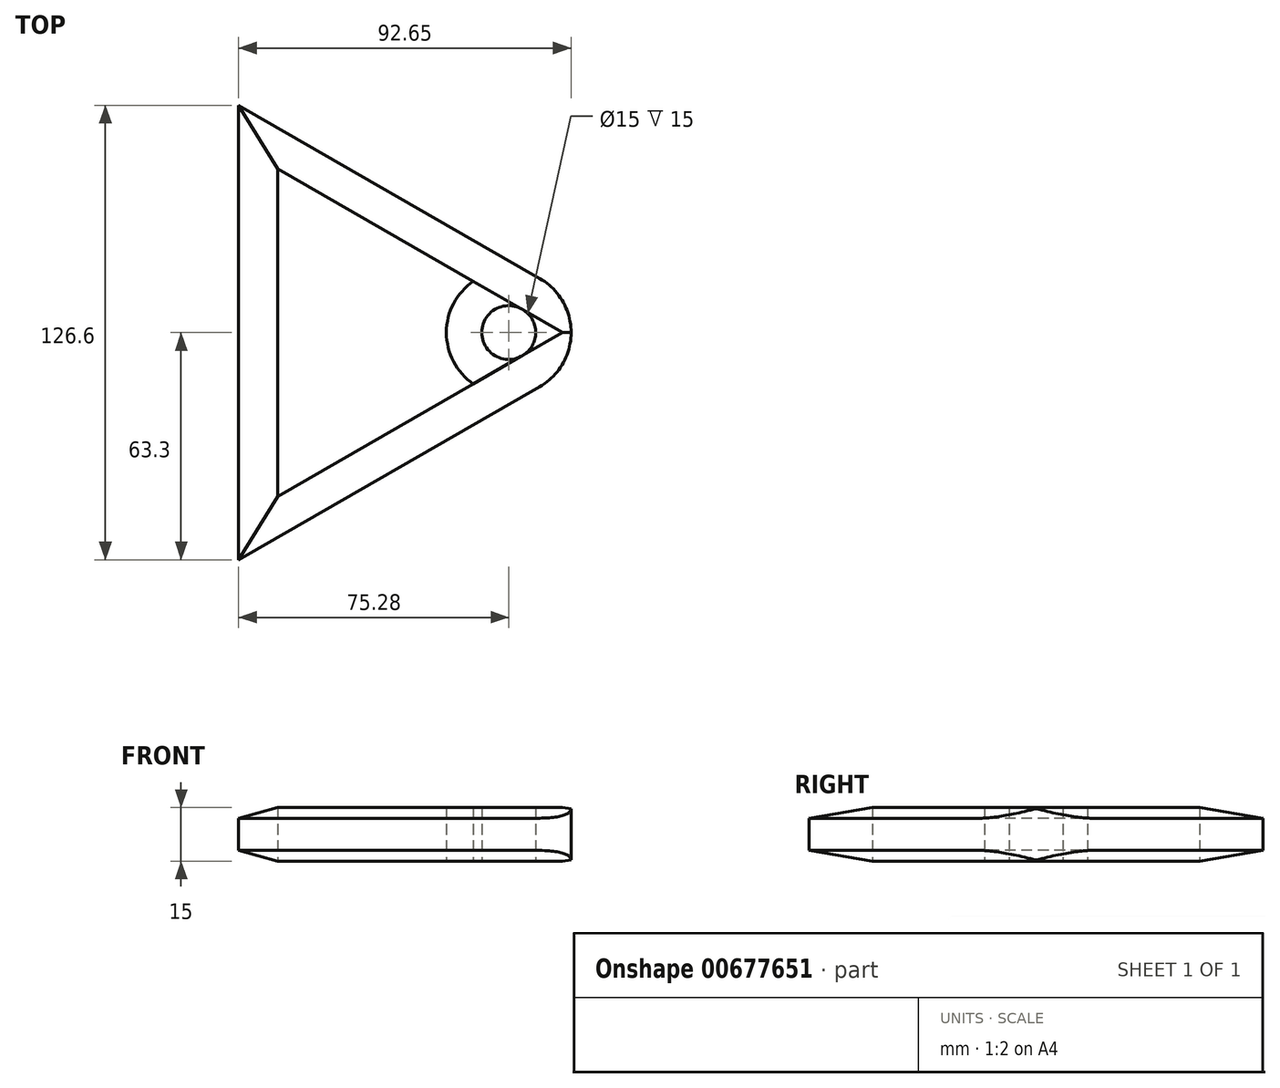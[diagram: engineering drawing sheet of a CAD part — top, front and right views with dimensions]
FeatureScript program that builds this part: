
annotation { "Feature Type Name" : "Feature", "Feature Type Description" : "" }
export const myFeature = defineFeature(function(context is Context, id is Id, definition is map)
    precondition{}
    {
        {
            var Q0;
            Q0=qCreatedBy(makeId("Top.planeOp"),FACE);
            var sketch = newSketch(context, id + "F0", { "sketchPlane" : qUnion([Q0])});
            skLineSegment(sketch, "E0", {"start": v(0, 0) * mm, "end": v(0, 63.3) * mm});
            skArc(sketch, "E1", {"start": v(82.78, 0) * mm, "mid": v(75.28, 7.5) * mm, "end": v(67.78, 0) * mm});
            skArc(sketch, "E2", {"start": v(65.42, 14.3) * mm, "mid": v(59.9, 8.08) * mm, "end": v(57.9, 0) * mm});
            skLineSegment(sketch, "E3", {"start": v(0, 63.3) * mm, "end": v(83.94, 15.06) * mm});
            skLineSegment(sketch, "E4", {"start": v(10.9, 45.64) * mm, "end": v(65.42, 14.3) * mm});
            skLineSegment(sketch, "E5", {"start": v(10.9, 45.64) * mm, "end": v(10.9, 0) * mm});
            skLineSegment(sketch, "E6", {"start": v(0, 0) * mm, "end": v(10.9, 0) * mm});
            skLineSegment(sketch, "E7", {"start": v(57.9, 0) * mm, "end": v(67.78, 0) * mm});
            skArc(sketch, "E8.trimOffspring", {"start": v(92.65, 0) * mm, "mid": v(90.32, 8.7) * mm, "end": v(83.94, 15.06) * mm});
            skPoint(sketch, "E9.orphan", {"position": v(38.05, 0) * mm});
            skLineSegment(sketch, "E10.trimOffspring", {"start": v(82.78, 0) * mm, "end": v(92.65, 0) * mm});
            skSolve(sketch);
        }
        {
            var Q0;
            Q0=makeQuery(id+"F0.imprint","IMPRINT",FACE,{"disambiguationData":[TD([[makeQuery(id+"F0.imprint","IMPRINT",EDGE,{"derivedFrom":sQuery(id+"F0.wireOp",EDGE,"E0")}),-1.0]])]});
            extrude(context, id + "F1", {"entities" : qUnion([Q0]), "depth" : 15 * mm, "offsetDistance" : 25.4 * mm});
        }
        {
            var Q0;
            Q0=makeQuery(id+"F1.opExtrude","SWEPT_FACE",FACE,{"disambiguationData":[OSD([sQuery(id+"F0.wireOp",EDGE,"E6")])]});
            var sketch = newSketch(context, id + "F2", { "sketchPlane" : qUnion([Q0])});
            skLineSegment(sketch, "E11", {"start": v(0, 12) * mm, "end": v(10.9, 15) * mm});
            skLineSegment(sketch, "E12", {"start": v(10.9, 15) * mm, "end": v(0, 15) * mm});
            skLineSegment(sketch, "E13", {"start": v(0, 15) * mm, "end": v(0, 12) * mm});
            skLineSegment(sketch, "E14", {"start": v(10.9, 0) * mm, "end": v(0, 0) * mm});
            skLineSegment(sketch, "E15", {"start": v(0, 0) * mm, "end": v(0, 3) * mm});
            skLineSegment(sketch, "E16", {"start": v(0, 3) * mm, "end": v(10.9, 0) * mm});
            skSolve(sketch);
        }
        {
            var Q0;
            Q0 = qSketchRegion(id + "F2", true);
            extrude(context, id + "F3", {"entities" : qUnion([Q0]), "operationType" : NewBodyOperationType.REMOVE, "oppositeDirection" : true, "depth" : 277.88 * mm, "offsetDistance" : 25.4 * mm});
        }
        {
            var Q0;
            Q0=makeQuery(id+"F1.opExtrude","CAP_EDGE",EDGE,{"disambiguationData":[OSD([sQuery(id+"F0.wireOp",EDGE,"E4")])],"isStart":false});
            cPlane(context, id + "F4", {"entities" : qUnion([Q0]), "cplaneType" : CPlaneType.MID_PLANE, "offset" : 25.4 * mm, "width" : 152.4 * mm, "height" : 152.4 * mm});
        }
        {
            var Q0;
            Q0=qCreatedBy(id+"F4.planeOp",FACE);
            var sketch = newSketch(context, id + "F5", { "sketchPlane" : qUnion([Q0])});
            skLineSegment(sketch, "E17", {"start": v(54.88, 12) * mm, "end": v(54.88, 15) * mm});
            skLineSegment(sketch, "E18", {"start": v(54.88, 15) * mm, "end": v(45, 15) * mm});
            skLineSegment(sketch, "E19", {"start": v(45, 15) * mm, "end": v(54.88, 12) * mm});
            skLineSegment(sketch, "E20", {"start": v(45, 0) * mm, "end": v(54.88, 0) * mm});
            skLineSegment(sketch, "E21", {"start": v(54.88, 0) * mm, "end": v(54.88, 3) * mm});
            skLineSegment(sketch, "E22", {"start": v(54.88, 3) * mm, "end": v(45, 0) * mm});
            skSolve(sketch);
        }
        {
            var Q0;
            Q0 = qSketchRegion(id + "F5", true);
            extrude(context, id + "F6", {"entities" : qUnion([Q0]), "operationType" : NewBodyOperationType.REMOVE, "oppositeDirection" : true, "depth" : 239.27 * mm, "offsetDistance" : 25.4 * mm, "hasSecondDirection" : true, "secondDirectionOppositeDirection" : false, "secondDirectionDepth" : 316.74 * mm});
        }
        {
            var Q0;
            Q0=makeQuery(id+"F1.opExtrude","SWEPT_BODY",BODY,{"disambiguationData":[OSD([sQuery(id+"F0.wireOp",EDGE,"E0"),sQuery(id+"F0.wireOp",EDGE,"E1"),sQuery(id+"F0.wireOp",EDGE,"E2"),sQuery(id+"F0.wireOp",EDGE,"E3"),sQuery(id+"F0.wireOp",EDGE,"E4"),sQuery(id+"F0.wireOp",EDGE,"E5"),sQuery(id+"F0.wireOp",EDGE,"E6"),sQuery(id+"F0.wireOp",EDGE,"E7"),sQuery(id+"F0.wireOp",EDGE,"E8.trimOffspring"),sQuery(id+"F0.wireOp",EDGE,"E10.trimOffspring")])]});
            var Q1;
            Q1=qCreatedBy(makeId("Front.planeOp"),FACE);
            mirror(context, id + "F7", {"operationType" : NewBodyOperationType.ADD, "entities" : qUnion([Q0]), "mirrorPlane" : qUnion([Q1])});
        }
    });
